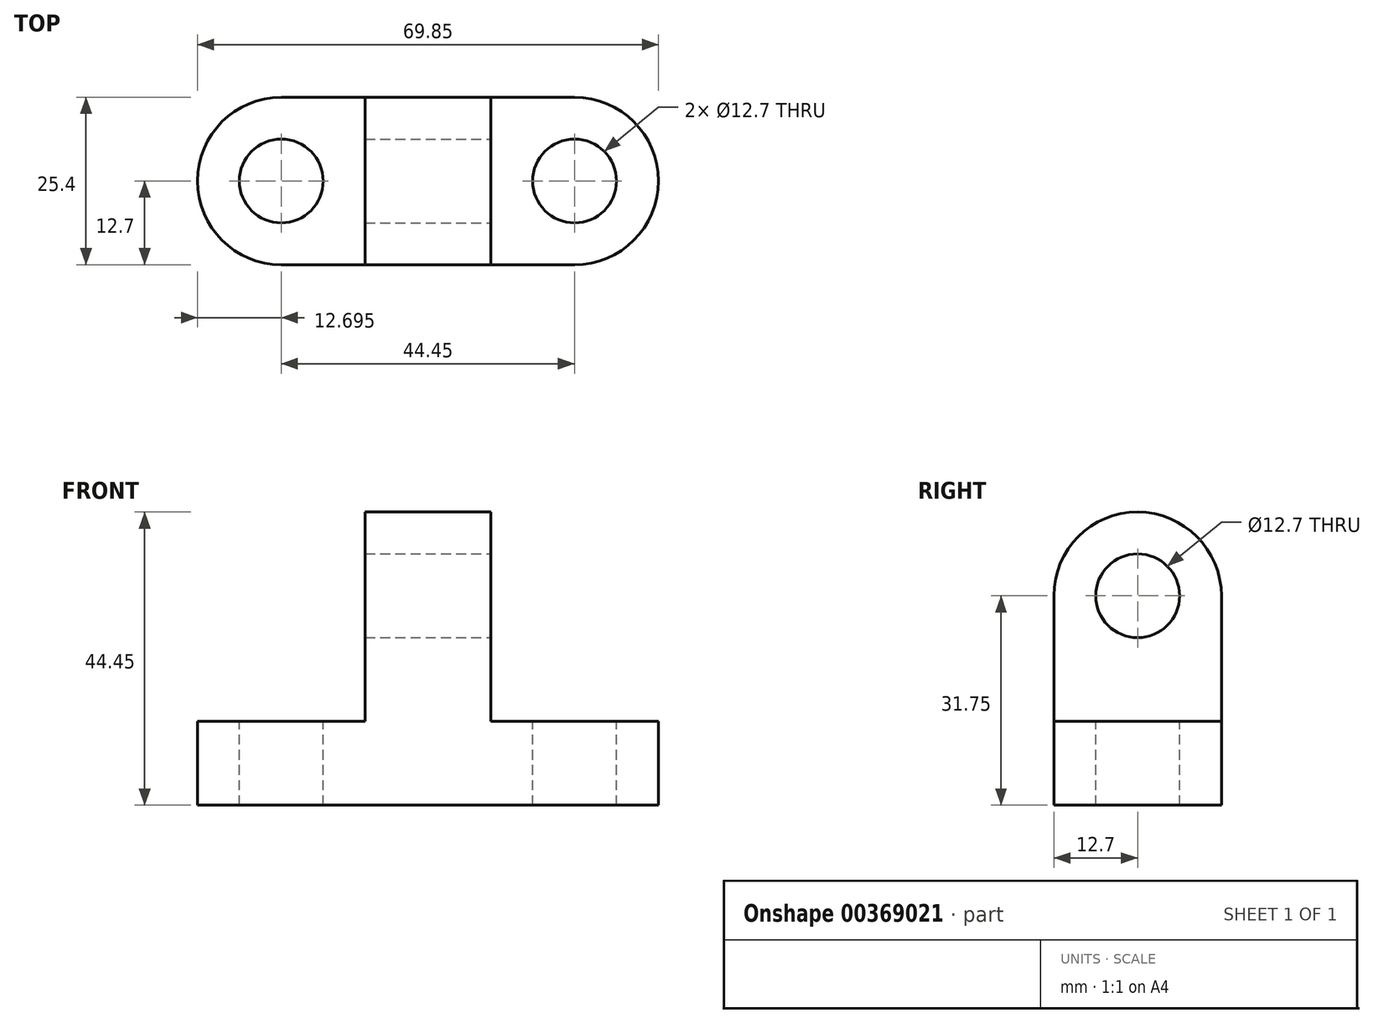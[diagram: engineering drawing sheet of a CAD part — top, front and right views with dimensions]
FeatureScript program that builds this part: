
annotation { "Feature Type Name" : "Feature", "Feature Type Description" : "" }
export const myFeature = defineFeature(function(context is Context, id is Id, definition is map)
    precondition{}
    {
        {
            var Q0;
            Q0=qCreatedBy(makeId("Front.planeOp"),FACE);
            var sketch = newSketch(context, id + "F0", { "sketchPlane" : qUnion([Q0])});
            skLineSegment(sketch, "E0", {"start": v(-24.9, 0) * mm, "end": v(-24.9, 44.45) * mm});
            skLineSegment(sketch, "E1", {"start": v(-24.9, 44.45) * mm, "end": v(44.95, 44.45) * mm});
            skLineSegment(sketch, "E2", {"start": v(44.95, 44.45) * mm, "end": v(44.95, 0) * mm});
            skLineSegment(sketch, "E3", {"start": v(-24.9, 0) * mm, "end": v(44.95, 0) * mm});
            skSolve(sketch);
        }
        {
            var Q0;
            Q0=makeQuery(id+"F0.imprint","IMPRINT",FACE,{"disambiguationData":[TD([[makeQuery(id+"F0.imprint","IMPRINT",EDGE,{"derivedFrom":sQuery(id+"F0.wireOp",EDGE,"E0")}),-1.0]])]});
            extrude(context, id + "F1", {"entities" : qUnion([Q0]), "depth" : 25.4 * mm});
        }
        {
            var Q0;
            Q0=makeQuery(id+"F1.opExtrude","SWEPT_FACE",FACE,{"disambiguationData":[OSD([sQuery(id+"F0.wireOp",EDGE,"E2")])]});
            var sketch = newSketch(context, id + "F2", { "sketchPlane" : qUnion([Q0])});
            skCircle(sketch, "E4", {"center": v(-12.7, 31.75) * mm, "radius": 6.35 * mm});
            skPoint(sketch, "E4.centerSnap0", {"position": v(-12.7, 44.45) * mm});
            skPoint(sketch, "E5", {"position": v(-25.4, 31.75) * mm});
            skArc(sketch, "E6", {"start": v(-12.7, 44.45) * mm, "mid": v(-21.68, 40.73) * mm, "end": v(-25.4, 31.75) * mm});
            skArc(sketch, "E7", {"start": v(0, 31.75) * mm, "mid": v(-3.72, 40.73) * mm, "end": v(-12.7, 44.45) * mm});
            skSolve(sketch);
        }
        {
            var Q0;
            Q0=makeQuery(id+"F2.imprint","IMPRINT",FACE,{"disambiguationData":[TD([[makeQuery(id+"F2.imprint","IMPRINT",EDGE,{"derivedFrom":sQuery(id+"F2.wireOp",EDGE,"E4")}),1.0]])]});
            extrude(context, id + "F3", {"entities" : qUnion([Q0]), "operationType" : NewBodyOperationType.REMOVE, "oppositeDirection" : true, "depth" : 69.85 * mm});
        }
        {
            var Q0;
            Q0=makeQuery(id+"F1.opExtrude","SWEPT_FACE",FACE,{"disambiguationData":[OSD([sQuery(id+"F0.wireOp",EDGE,"E1")])]});
            var sketch = newSketch(context, id + "F4", { "sketchPlane" : qUnion([Q0])});
            skCircle(sketch, "E8", {"center": v(-12.2, -12.7) * mm, "radius": 6.35 * mm});
            skPoint(sketch, "E8.centerSnap0", {"position": v(-24.9, -12.7) * mm});
            skCircle(sketch, "E9", {"center": v(32.25, -12.7) * mm, "radius": 6.35 * mm});
            skSolve(sketch);
        }
        {
            var Q0;
            Q0=makeQuery(id+"F4.imprint","IMPRINT",FACE,{"disambiguationData":[TD([[makeQuery(id+"F4.imprint","IMPRINT",EDGE,{"derivedFrom":sQuery(id+"F4.wireOp",EDGE,"E8")}),1.0]])]});
            var Q1;
            Q1=makeQuery(id+"F4.imprint","IMPRINT",FACE,{"disambiguationData":[TD([[makeQuery(id+"F4.imprint","IMPRINT",EDGE,{"derivedFrom":sQuery(id+"F4.wireOp",EDGE,"E9")}),1.0]])]});
            extrude(context, id + "F5", {"entities" : qUnion([Q0, Q1]), "operationType" : NewBodyOperationType.REMOVE, "oppositeDirection" : true, "depth" : 50.8 * mm});
        }
        {
            var Q0;
            {var subQ0=sQuery(id+"F2.wireOp",EDGE,"E6");var subQ1=sQuery(id+"F0.wireOp",EDGE,"E2");var subQ2=makeQuery(id+"F1.opExtrude","CAP_EDGE",EDGE,{"disambiguationData":[OSD([subQ1])],"isStart":false});var subQ3=makeQuery(id+"F2.imprint","INTERSECT",VERTEX,{"derivedFrom":[subQ2,subQ0]});Q0=makeQuery(id+"F2.imprint","IMPRINT",FACE,{"disambiguationData":[TD([[makeQuery(id+"F2.imprint","IMPRINT",EDGE,{"disambiguationData":[TD([[subQ3,1.0]])],"derivedFrom":subQ0}),-1.0]])]});}
            var Q1;
            {var subQ0=sQuery(id+"F2.wireOp",EDGE,"E7");Q1=makeQuery(id+"F2.imprint","IMPRINT",FACE,{"disambiguationData":[TD([[makeQuery(id+"F2.imprint","IMPRINT",EDGE,{"derivedFrom":subQ0}),-1.0]])]});}
            extrude(context, id + "F6", {"entities" : qUnion([Q0, Q1]), "operationType" : NewBodyOperationType.REMOVE, "oppositeDirection" : true, "depth" : 69.85 * mm});
        }
        {
            var Q0;
            Q0=makeQuery(id+"F1.opExtrude","SWEPT_FACE",FACE,{"disambiguationData":[OSD([sQuery(id+"F0.wireOp",EDGE,"E2")])]});
            var sketch = newSketch(context, id + "F7", { "sketchPlane" : qUnion([Q0])});
            skLineSegment(sketch, "E10", {"start": v(-25.4, 12.7) * mm, "end": v(0, 12.7) * mm});
            skSolve(sketch);
        }
        {
            var Q0;
            {var subQ2=sQuery(id+"F7.wireOp",EDGE,"E10");Q0=makeQuery(id+"F7.imprint","IMPRINT",FACE,{"disambiguationData":[TD([[makeQuery(id+"F7.imprint","IMPRINT",EDGE,{"derivedFrom":subQ2}),1.0]])]});}
            extrude(context, id + "F8", {"entities" : qUnion([Q0]), "operationType" : NewBodyOperationType.REMOVE, "oppositeDirection" : true, "depth" : 25.4 * mm});
        }
        {
            var Q0;
            Q0=makeQuery(id+"F1.opExtrude","SWEPT_FACE",FACE,{"disambiguationData":[OSD([sQuery(id+"F0.wireOp",EDGE,"E0")])]});
            var sketch = newSketch(context, id + "F9", { "sketchPlane" : qUnion([Q0])});
            skLineSegment(sketch, "E11", {"start": v(0, 12.7) * mm, "end": v(25.4, 12.7) * mm});
            skSolve(sketch);
        }
        {
            var Q0;
            {var subQ2=sQuery(id+"F9.wireOp",EDGE,"E11");Q0=makeQuery(id+"F9.imprint","IMPRINT",FACE,{"disambiguationData":[TD([[makeQuery(id+"F9.imprint","IMPRINT",EDGE,{"derivedFrom":subQ2}),1.0]])]});}
            extrude(context, id + "F10", {"entities" : qUnion([Q0]), "operationType" : NewBodyOperationType.REMOVE, "oppositeDirection" : true, "depth" : 25.4 * mm});
        }
        {
            var Q0;
            Q0=makeQuery(id+"F8.boolean.opBoolean","COPY",FACE,{"derivedFrom":makeQuery(id+"F8.opExtrude","SWEPT_FACE",FACE,{"disambiguationData":[OSD([sQuery(id+"F7.wireOp",EDGE,"E10")])]})});
            var sketch = newSketch(context, id + "F11", { "sketchPlane" : qUnion([Q0])});
            skPoint(sketch, "E12", {"position": v(44.95, -12.7) * mm});
            skPoint(sketch, "E13", {"position": v(32.25, 0) * mm});
            skPoint(sketch, "E14", {"position": v(32.25, -25.4) * mm});
            skArc(sketch, "E15", {"start": v(44.95, -12.7) * mm, "mid": v(41.23, -3.72) * mm, "end": v(32.25, 0) * mm});
            skArc(sketch, "E16", {"start": v(32.25, -25.4) * mm, "mid": v(41.23, -21.68) * mm, "end": v(44.95, -12.7) * mm});
            skSolve(sketch);
        }
        {
            var Q0;
            {var subQ0=sQuery(id+"F11.wireOp",EDGE,"E15");Q0=makeQuery(id+"F11.imprint","IMPRINT",FACE,{"disambiguationData":[TD([[makeQuery(id+"F11.imprint","IMPRINT",EDGE,{"derivedFrom":subQ0}),-1.0]])]});}
            var Q1;
            {var subQ0=sQuery(id+"F11.wireOp",EDGE,"E16");Q1=makeQuery(id+"F11.imprint","IMPRINT",FACE,{"disambiguationData":[TD([[makeQuery(id+"F11.imprint","IMPRINT",EDGE,{"derivedFrom":subQ0}),-1.0]])]});}
            extrude(context, id + "F12", {"entities" : qUnion([Q0, Q1]), "operationType" : NewBodyOperationType.REMOVE, "oppositeDirection" : true, "depth" : 25.4 * mm});
        }
        {
            var Q0;
            Q0=makeQuery(id+"F10.boolean.opBoolean","COPY",FACE,{"derivedFrom":makeQuery(id+"F10.opExtrude","SWEPT_FACE",FACE,{"disambiguationData":[OSD([sQuery(id+"F9.wireOp",EDGE,"E11")])]})});
            var sketch = newSketch(context, id + "F13", { "sketchPlane" : qUnion([Q0])});
            skPoint(sketch, "E17", {"position": v(-24.9, -12.7) * mm});
            skPoint(sketch, "E18", {"position": v(-12.2, 0) * mm});
            skArc(sketch, "E19", {"start": v(-12.2, 0) * mm, "mid": v(-21.18, -3.72) * mm, "end": v(-24.9, -12.7) * mm});
            skArc(sketch, "E20", {"start": v(-24.9, -12.7) * mm, "mid": v(-21.18, -21.68) * mm, "end": v(-12.2, -25.4) * mm});
            skSolve(sketch);
        }
        {
            var Q0;
            {var subQ0=sQuery(id+"F13.wireOp",EDGE,"E19");Q0=makeQuery(id+"F13.imprint","IMPRINT",FACE,{"disambiguationData":[TD([[makeQuery(id+"F13.imprint","IMPRINT",EDGE,{"derivedFrom":subQ0}),-1.0]])]});}
            var Q1;
            {var subQ0=sQuery(id+"F13.wireOp",EDGE,"E20");Q1=makeQuery(id+"F13.imprint","IMPRINT",FACE,{"disambiguationData":[TD([[makeQuery(id+"F13.imprint","IMPRINT",EDGE,{"derivedFrom":subQ0}),-1.0]])]});}
            extrude(context, id + "F14", {"entities" : qUnion([Q0, Q1]), "operationType" : NewBodyOperationType.REMOVE, "oppositeDirection" : true, "depth" : 25.4 * mm});
        }
    });
